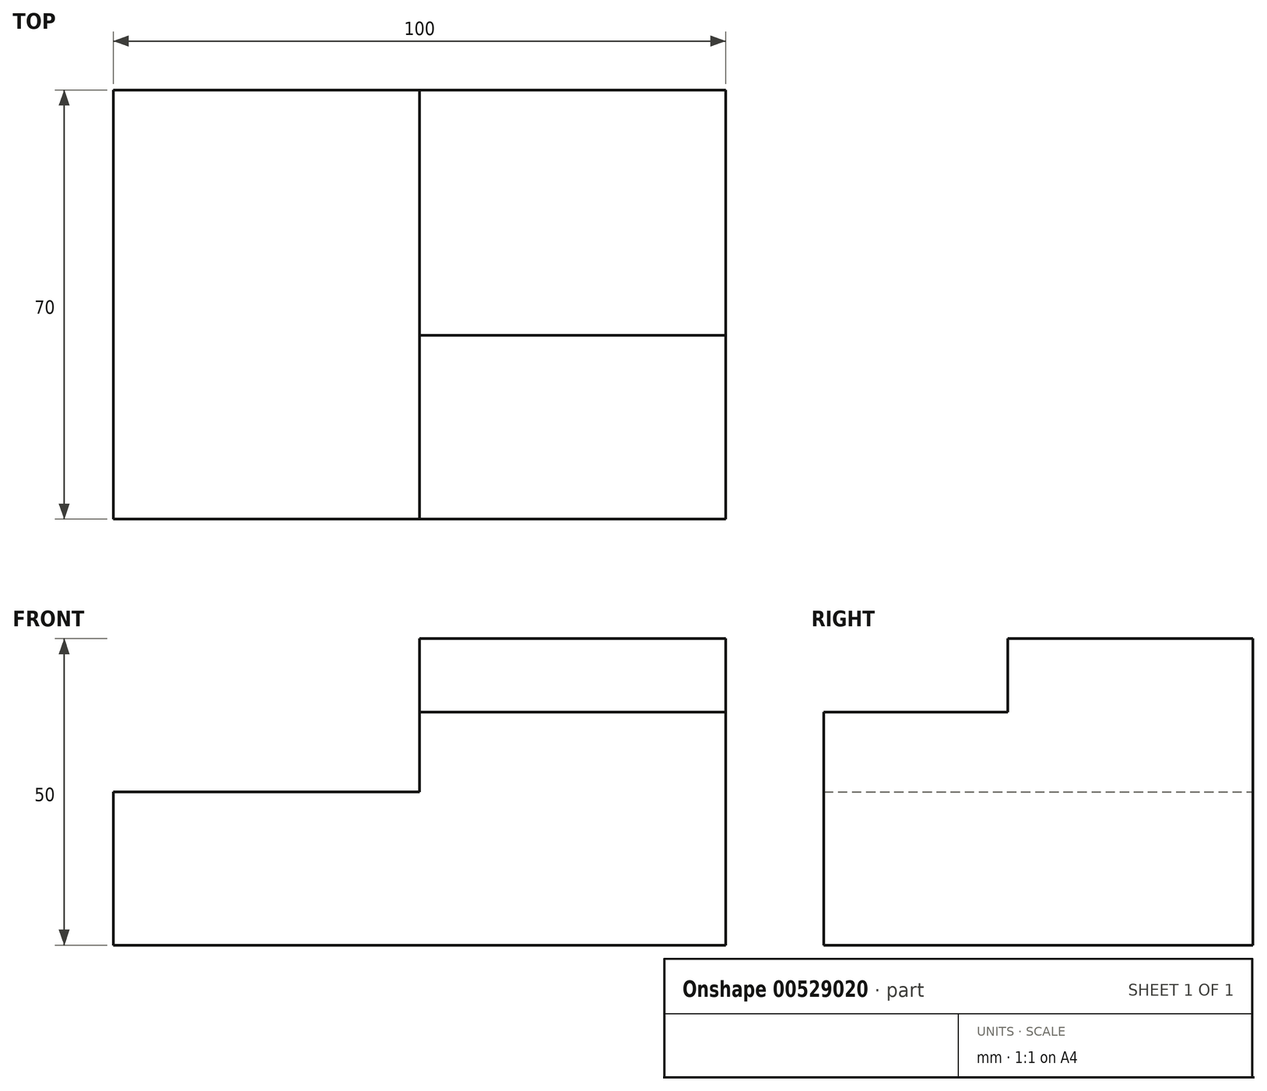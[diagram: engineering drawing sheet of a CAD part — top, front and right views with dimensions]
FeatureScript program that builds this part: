
annotation { "Feature Type Name" : "Feature", "Feature Type Description" : "" }
export const myFeature = defineFeature(function(context is Context, id is Id, definition is map)
    precondition{}
    {
        {
            var Q0;
            Q0=qCreatedBy(makeId("Front.planeOp"),FACE);
            var sketch = newSketch(context, id + "F0", { "sketchPlane" : qUnion([Q0])});
            skLineSegment(sketch, "E0", {"start": v(-51.43, 0) * mm, "end": v(48.57, 0) * mm});
            skLineSegment(sketch, "E1", {"start": v(48.57, 0) * mm, "end": v(48.57, 38) * mm});
            skLineSegment(sketch, "E2", {"start": v(48.57, 38) * mm, "end": v(48.57, 50) * mm});
            skLineSegment(sketch, "E3", {"start": v(48.57, 50) * mm, "end": v(-1.43, 50) * mm});
            skLineSegment(sketch, "E4", {"start": v(-1.43, 50) * mm, "end": v(-1.43, 38) * mm});
            skLineSegment(sketch, "E5", {"start": v(-1.43, 38) * mm, "end": v(-1.43, 25) * mm});
            skLineSegment(sketch, "E6", {"start": v(-1.43, 25) * mm, "end": v(-51.43, 25) * mm});
            skLineSegment(sketch, "E7", {"start": v(-51.43, 25) * mm, "end": v(-51.43, 0) * mm});
            skLineSegment(sketch, "E8", {"start": v(-1.43, 38) * mm, "end": v(48.57, 38) * mm});
            skSolve(sketch);
        }
        {
            var Q0;
            Q0=makeQuery(id+"F0.imprint","IMPRINT",FACE,{"disambiguationData":[TD([[makeQuery(id+"F0.imprint","IMPRINT",EDGE,{"derivedFrom":sQuery(id+"F0.wireOp",EDGE,"E0")}),1.0]])]});
            extrude(context, id + "F1", {"entities" : qUnion([Q0]), "depth" : 70 * mm, "offsetDistance" : 25 * mm});
        }
        {
            var Q0;
            Q0 = qSketchRegion(id + "F0", true);
            extrude(context, id + "F2", {"entities" : qUnion([Q0]), "operationType" : NewBodyOperationType.ADD, "depth" : 40 * mm, "offsetDistance" : 25 * mm});
        }
    });
